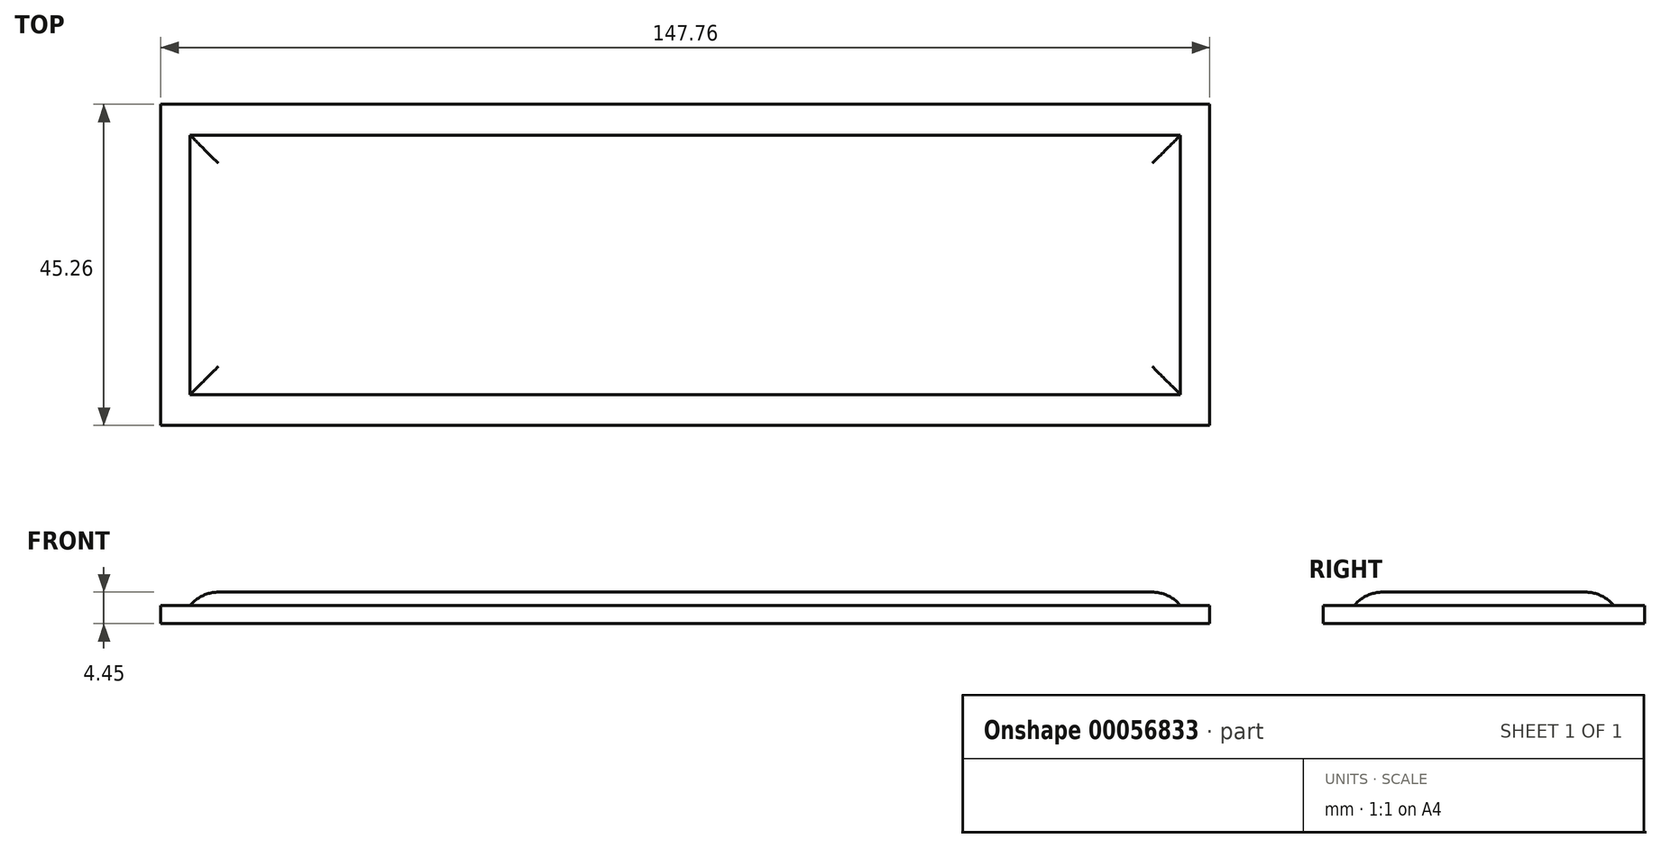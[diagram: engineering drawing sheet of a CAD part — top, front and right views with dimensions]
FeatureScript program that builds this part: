
annotation { "Feature Type Name" : "Feature", "Feature Type Description" : "" }
export const myFeature = defineFeature(function(context is Context, id is Id, definition is map)
    precondition{}
    {
        {
            var Q0;
            Q0=qCreatedBy(makeId("Top.planeOp"),FACE);
            var sketch = newSketch(context, id + "F0", { "sketchPlane" : qUnion([Q0])});
            skLineSegment(sketch, "E0.rect.bottom", {"start": v(73.88, -22.63) * mm, "end": v(-73.88, -22.63) * mm});
            skLineSegment(sketch, "E0.rect.top", {"start": v(73.88, 22.63) * mm, "end": v(-73.88, 22.63) * mm});
            skLineSegment(sketch, "E0.rect.left", {"start": v(73.88, -22.63) * mm, "end": v(73.88, 22.63) * mm});
            skLineSegment(sketch, "E0.rect.right", {"start": v(-73.88, -22.63) * mm, "end": v(-73.88, 22.63) * mm});
            skPoint(sketch, "E0.rect.middle", {"position": v(0, 0) * mm});
            skSolve(sketch);
        }
        {
            var Q0;
            Q0=makeQuery(id+"F0.imprint","IMPRINT",FACE,{"disambiguationData":[TD([[makeQuery(id+"F0.imprint","IMPRINT",EDGE,{"derivedFrom":sQuery(id+"F0.wireOp",EDGE,"E0.rect.bottom")}),-1.0]])]});
            extrude(context, id + "F1", {"entities" : qUnion([Q0]), "depth" : 2.54 * mm});
        }
        {
            var Q0;
            Q0=makeQuery(id+"F1.opExtrude","CAP_FACE",FACE,{"disambiguationData":[OSD([sQuery(id+"F0.wireOp",EDGE,"E0.rect.bottom"),sQuery(id+"F0.wireOp",EDGE,"E0.rect.top"),sQuery(id+"F0.wireOp",EDGE,"E0.rect.left"),sQuery(id+"F0.wireOp",EDGE,"E0.rect.right")])],"isStart":false});
            var sketch = newSketch(context, id + "F2", { "sketchPlane" : qUnion([Q0])});
            skLineSegment(sketch, "E1.rect.bottom", {"start": v(69.76, -18.28) * mm, "end": v(-69.76, -18.28) * mm});
            skLineSegment(sketch, "E1.rect.top", {"start": v(69.76, 18.28) * mm, "end": v(-69.76, 18.28) * mm});
            skLineSegment(sketch, "E1.rect.left", {"start": v(69.76, -18.28) * mm, "end": v(69.76, 18.28) * mm});
            skLineSegment(sketch, "E1.rect.right", {"start": v(-69.76, -18.28) * mm, "end": v(-69.76, 18.28) * mm});
            skPoint(sketch, "E1.rect.middle", {"position": v(0, 0) * mm});
            skSolve(sketch);
        }
        {
            var Q0;
            Q0=makeQuery(id+"F2.imprint","IMPRINT",FACE,{"disambiguationData":[TD([[makeQuery(id+"F2.imprint","IMPRINT",EDGE,{"derivedFrom":sQuery(id+"F2.wireOp",EDGE,"E1.rect.bottom")}),-1.0]])]});
            extrude(context, id + "F3", {"entities" : qUnion([Q0]), "operationType" : NewBodyOperationType.ADD, "depth" : 1.9 * mm});
        }
        {
            var Q0;
            Q0=makeQuery(id+"F3.opExtrude","CAP_EDGE",EDGE,{"disambiguationData":[OSD([sQuery(id+"F2.wireOp",EDGE,"E1.rect.bottom")])],"isStart":false});
            var Q1;
            Q1=makeQuery(id+"F3.opExtrude","CAP_EDGE",EDGE,{"disambiguationData":[OSD([sQuery(id+"F2.wireOp",EDGE,"E1.rect.right")])],"isStart":false});
            var Q2;
            Q2=makeQuery(id+"F3.opExtrude","CAP_EDGE",EDGE,{"disambiguationData":[OSD([sQuery(id+"F2.wireOp",EDGE,"E1.rect.top")])],"isStart":false});
            var Q3;
            Q3=makeQuery(id+"F3.opExtrude","CAP_EDGE",EDGE,{"disambiguationData":[OSD([sQuery(id+"F2.wireOp",EDGE,"E1.rect.left")])],"isStart":false});
            fillet(context, id + "F4", {"entities" : qUnion([Q0, Q1, Q2, Q3]), "radius" : 5.08 * mm, "tangentPropagation" : true, "allowEdgeOverflow" : false});
        }
    });
